# Revit family: BB-100.BIM
name_source: partatom
category: Fire Alarm Devices
units: mm (PartAtom-declared; Revit-internal decimal feet)

## family parameters
Cut with Voids When Loaded = No
Host = Face
Maintain Annotation Orientation = Yes
OmniClass Number = 23.85.30.21.11
OmniClass Title = Fire Detection, Monitoring and Alarm
Part Type = Normal
Room Calculation Point = No
Round Connector Dimension = Use Diameter
Shared = Yes

## types (2) — shared parameters
Assembly Code = D5030700
Default Elevation = 5' - 6"
Electrical Connector 1 = Power Only
Height = 0' - 0"
Length = 2' - 6 11/32"
Manufacturer = Notifier
URL = www.notifier.com
Width = 1' - 10 1/2"

## per-type parameters (varying)
| type | Cabinet Finish | Description | Model |
| BB Series 100 Black | Metal_Notifier_Cabinet-Black | Battery Box-Black | BB-100 |
| BB Series 100 Red | Plastic_Notifier_Cabinet-Red | Battery Box-Red | BB-100R |

## geometry (parser evidence)
native form markers: Blend x8, Sweep x2
no freeform markers — native parametric forms only
